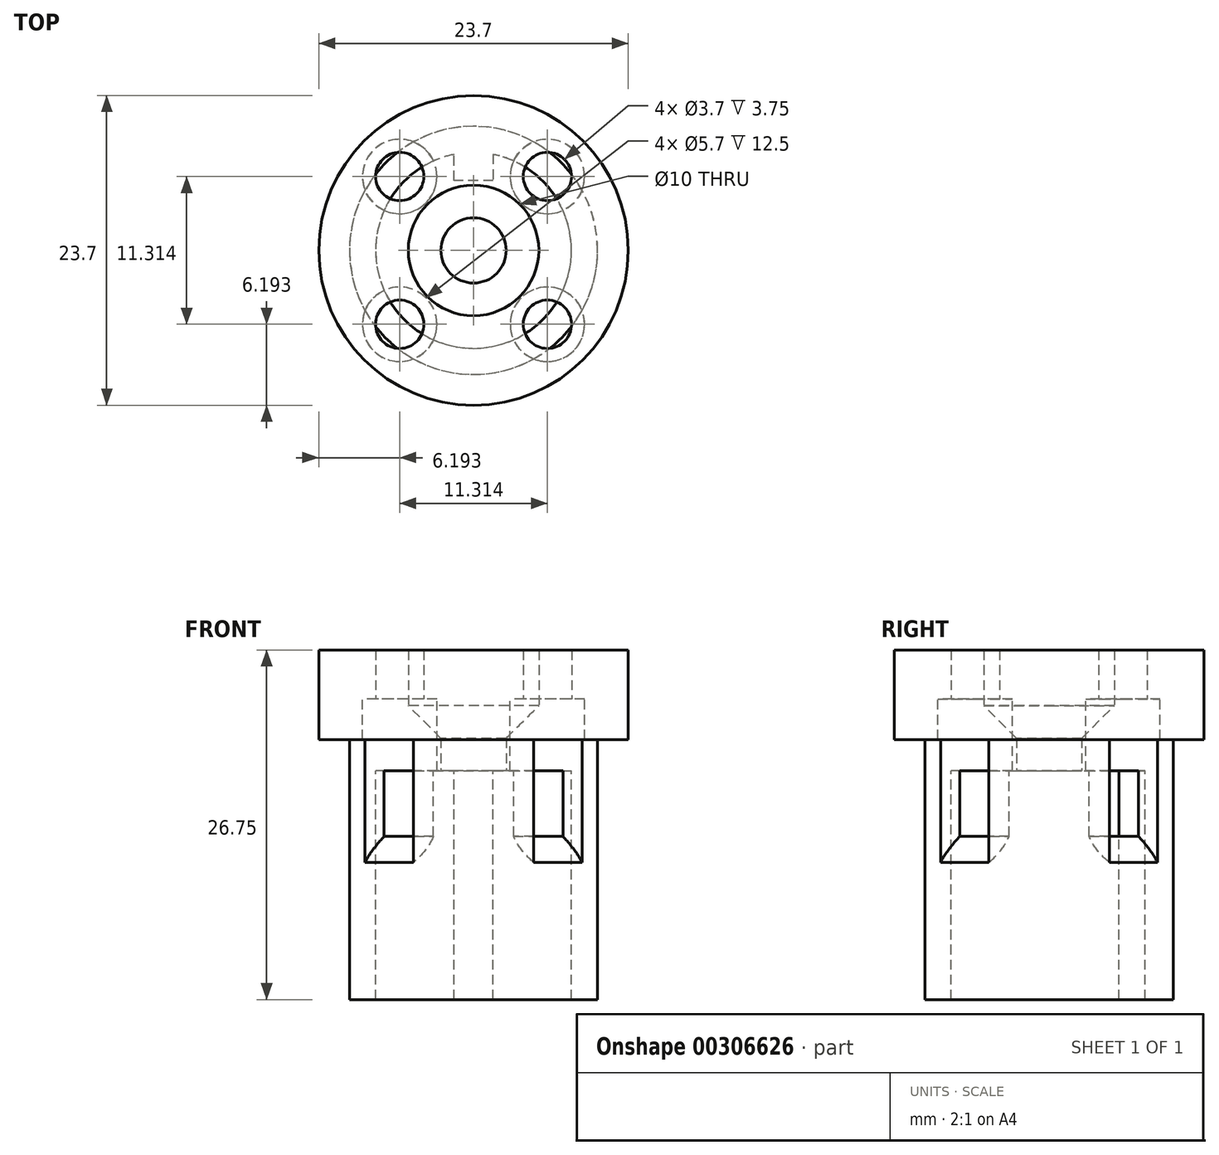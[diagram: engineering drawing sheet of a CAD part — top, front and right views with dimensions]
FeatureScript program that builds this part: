
annotation { "Feature Type Name" : "Feature", "Feature Type Description" : "" }
export const myFeature = defineFeature(function(context is Context, id is Id, definition is map)
    precondition{}
    {
        {
            var Q0;
            Q0=qCreatedBy(makeId("Top.planeOp"),FACE);
            var sketch = newSketch(context, id + "F0", { "sketchPlane" : qUnion([Q0])});
            skCircle(sketch, "E0", {"center": v(0, 0) * mm, "radius": 7.5 * mm});
            skPoint(sketch, "E1", {"position": v(-1.5, 7.35) * mm});
            skPoint(sketch, "E2", {"position": v(1.5, 7.35) * mm});
            skLineSegment(sketch, "E3", {"start": v(-1.5, 7.35) * mm, "end": v(1.5, 7.35) * mm});
            skPoint(sketch, "E4", {"position": v(0, 7.35) * mm});
            skLineSegment(sketch, "E5", {"start": v(-1.5, 7.35) * mm, "end": v(-1.5, 5.35) * mm});
            skLineSegment(sketch, "E6", {"start": v(-1.5, 5.35) * mm, "end": v(1.5, 5.35) * mm});
            skLineSegment(sketch, "E7", {"start": v(1.5, 5.35) * mm, "end": v(1.5, 7.35) * mm});
            skCircle(sketch, "E8", {"center": v(0, 0) * mm, "radius": 2.5 * mm});
            skCircle(sketch, "E9", {"center": v(0, 0) * mm, "radius": 9.5 * mm});
            skSolve(sketch);
        }
        {
            var Q0;
            Q0=qCreatedBy(makeId("Top.planeOp"),FACE);
            var sketch = newSketch(context, id + "F1", { "sketchPlane" : qUnion([Q0])});
            skCircle(sketch, "E10", {"center": v(0, 0) * mm, "radius": 2.5 * mm});
            skLineSegment(sketch, "E11", {"start": v(-2, 1.5) * mm, "end": v(2, 1.5) * mm});
            skCircle(sketch, "E12", {"center": v(0, 0) * mm, "radius": 4.5 * mm});
            skSolve(sketch);
        }
        {
            var Q0;
            Q0=makeQuery(id+"F0.imprint","IMPRINT",FACE,{"disambiguationData":[TD([[makeQuery(id+"F0.imprint","IMPRINT",EDGE,{"derivedFrom":sQuery(id+"F0.wireOp",EDGE,"E9")}),1.0]])]});
            var Q1;
            {var subQ0=sQuery(id+"F0.wireOp",EDGE,"E3");Q1=makeQuery(id+"F0.imprint","IMPRINT",FACE,{"disambiguationData":[TD([[makeQuery(id+"F0.imprint","IMPRINT",EDGE,{"derivedFrom":subQ0}),1.0]])]});}
            var Q2;
            Q2=makeQuery(id+"F0.imprint","IMPRINT",FACE,{"disambiguationData":[TD([[makeQuery(id+"F0.imprint","IMPRINT",EDGE,{"derivedFrom":sQuery(id+"F0.wireOp",EDGE,"E3")}),-1.0]])]});
            extrude(context, id + "F2", {"entities" : qUnion([Q0, Q1, Q2]), "oppositeDirection" : true, "depth" : 20 * mm});
        }
        {
            var Q0;
            Q0=makeQuery(id+"F1.imprint","IMPRINT",FACE,{"disambiguationData":[TD([[makeQuery(id+"F1.imprint","IMPRINT",EDGE,{"derivedFrom":sQuery(id+"F1.wireOp",EDGE,"E12")}),1.0]])]});
            extrude(context, id + "F3", {"entities" : qUnion([Q0]), "operationType" : NewBodyOperationType.ADD, "depth" : 3 * mm});
        }
        {
            var Q0;
            {var subQ1=sQuery(id+"F0.wireOp",EDGE,"E5");Q0=makeQuery(id+"F0.imprint","IMPRINT",FACE,{"disambiguationData":[TD([[makeQuery(id+"F0.imprint","IMPRINT",EDGE,{"derivedFrom":subQ1}),-1.0]])]});}
            var Q1;
            {var subQ0=sQuery(id+"F0.wireOp",EDGE,"E3");Q1=makeQuery(id+"F0.imprint","IMPRINT",FACE,{"disambiguationData":[TD([[makeQuery(id+"F0.imprint","IMPRINT",EDGE,{"derivedFrom":subQ0}),1.0]])]});}
            var Q2;
            Q2=makeQuery(id+"F0.imprint","IMPRINT",FACE,{"disambiguationData":[TD([[makeQuery(id+"F0.imprint","IMPRINT",EDGE,{"derivedFrom":sQuery(id+"F0.wireOp",EDGE,"E3")}),-1.0]])]});
            extrude(context, id + "F4", {"entities" : qUnion([Q0, Q1, Q2]), "operationType" : NewBodyOperationType.ADD, "endBound" : BoundingType.SYMMETRIC, "depth" : 5 * mm});
        }
        {
            var Q0;
            Q0=makeQuery(id+"F3.opExtrude","CAP_FACE",FACE,{"disambiguationData":[OSD([sQuery(id+"F1.wireOp",EDGE,"E10"),sQuery(id+"F1.wireOp",EDGE,"E11"),sQuery(id+"F1.wireOp",EDGE,"E12")])],"isStart":false});
            var sketch = newSketch(context, id + "F5", { "sketchPlane" : qUnion([Q0])});
            skCircle(sketch, "E13", {"center": v(0, 0) * mm, "radius": 8 * mm});
            skCircle(sketch, "E14", {"center": v(0, 0) * mm, "radius": 4 * mm});
            skLineSegment(sketch, "E15", {"start": v(5.66, -5.66) * mm, "end": v(-5.66, 5.66) * mm, "construction": true});
            skLineSegment(sketch, "E16", {"start": v(-5.66, -5.66) * mm, "end": v(5.66, 5.66) * mm, "construction": true});
            skLineSegment(sketch, "E17", {"start": v(-8, 0) * mm, "end": v(8, 0) * mm, "construction": true});
            skCircle(sketch, "E18", {"center": v(-5.66, 5.66) * mm, "radius": 1.85 * mm});
            skCircle(sketch, "E19", {"center": v(5.66, 5.66) * mm, "radius": 1.85 * mm});
            skCircle(sketch, "E20", {"center": v(-5.66, -5.66) * mm, "radius": 1.85 * mm});
            skCircle(sketch, "E21", {"center": v(5.66, -5.66) * mm, "radius": 1.85 * mm});
            skCircle(sketch, "E22", {"center": v(0, 0) * mm, "radius": 11.85 * mm});
            skCircle(sketch, "E23", {"center": v(-5.66, 5.66) * mm, "radius": 2.85 * mm});
            skCircle(sketch, "E24", {"center": v(5.66, 5.66) * mm, "radius": 2.85 * mm});
            skCircle(sketch, "E25", {"center": v(-5.66, -5.66) * mm, "radius": 2.85 * mm});
            skCircle(sketch, "E26", {"center": v(5.66, -5.66) * mm, "radius": 2.85 * mm});
            skSolve(sketch);
        }
        {
            var Q0;
            Q0=makeQuery(id+"F5.imprint","IMPRINT",FACE,{"disambiguationData":[TD([[makeQuery(id+"F5.imprint","IMPRINT",EDGE,{"derivedFrom":makeQuery(id+"F3.opExtrude","CAP_EDGE",EDGE,{"disambiguationData":[OSD([sQuery(id+"F1.wireOp",EDGE,"E12")])],"isStart":false})}),-1.0]])]});
            var Q1;
            Q1=makeQuery(id+"F5.imprint","IMPRINT",FACE,{"disambiguationData":[TD([[makeQuery(id+"F5.imprint","IMPRINT",EDGE,{"derivedFrom":sQuery(id+"F5.wireOp",EDGE,"E22")}),1.0]])]});
            var Q2;
            {var subQ0=sQuery(id+"F5.wireOp",EDGE,"E23");var subQ1=sQuery(id+"F5.wireOp",EDGE,"E13");var subQ2=makeQuery(id+"F5.imprint","INTERSECT",VERTEX,{"disambiguationData":[OD(0.0)],"derivedFrom":[subQ1,subQ0]});Q2=makeQuery(id+"F5.imprint","IMPRINT",FACE,{"disambiguationData":[TD([[makeQuery(id+"F5.imprint","IMPRINT",EDGE,{"disambiguationData":[TD([[subQ2,-1.0]])],"derivedFrom":subQ1}),-1.0]])]});}
            var Q3;
            {var subQ0=sQuery(id+"F5.wireOp",EDGE,"E23");var subQ1=sQuery(id+"F5.wireOp",EDGE,"E13");var subQ2=makeQuery(id+"F5.imprint","INTERSECT",VERTEX,{"disambiguationData":[OD(0.0)],"derivedFrom":[subQ1,subQ0]});Q3=makeQuery(id+"F5.imprint","IMPRINT",FACE,{"disambiguationData":[TD([[makeQuery(id+"F5.imprint","IMPRINT",EDGE,{"disambiguationData":[TD([[subQ2,-1.0]])],"derivedFrom":subQ1}),1.0]])]});}
            var Q4;
            {var subQ0=sQuery(id+"F5.wireOp",EDGE,"E19");var subQ1=sQuery(id+"F5.wireOp",EDGE,"E13");var subQ2=makeQuery(id+"F5.imprint","INTERSECT",VERTEX,{"disambiguationData":[OD(0.0)],"derivedFrom":[subQ1,subQ0]});Q4=makeQuery(id+"F5.imprint","IMPRINT",FACE,{"disambiguationData":[TD([[makeQuery(id+"F5.imprint","IMPRINT",EDGE,{"disambiguationData":[TD([[subQ2,1.0]])],"derivedFrom":subQ1}),-1.0]])]});}
            var Q5;
            {var subQ0=sQuery(id+"F5.wireOp",EDGE,"E19");var subQ1=sQuery(id+"F5.wireOp",EDGE,"E13");var subQ2=makeQuery(id+"F5.imprint","INTERSECT",VERTEX,{"disambiguationData":[OD(0.0)],"derivedFrom":[subQ1,subQ0]});Q5=makeQuery(id+"F5.imprint","IMPRINT",FACE,{"disambiguationData":[TD([[makeQuery(id+"F5.imprint","IMPRINT",EDGE,{"disambiguationData":[TD([[subQ2,1.0]])],"derivedFrom":subQ1}),1.0]])]});}
            var Q6;
            {var subQ0=sQuery(id+"F5.wireOp",EDGE,"E26");var subQ1=sQuery(id+"F5.wireOp",EDGE,"E13");var subQ2=makeQuery(id+"F5.imprint","INTERSECT",VERTEX,{"disambiguationData":[OD(0.0)],"derivedFrom":[subQ1,subQ0]});Q6=makeQuery(id+"F5.imprint","IMPRINT",FACE,{"disambiguationData":[TD([[makeQuery(id+"F5.imprint","IMPRINT",EDGE,{"disambiguationData":[TD([[subQ2,-1.0]])],"derivedFrom":subQ1}),-1.0]])]});}
            var Q7;
            {var subQ0=sQuery(id+"F5.wireOp",EDGE,"E26");var subQ1=sQuery(id+"F5.wireOp",EDGE,"E13");var subQ2=makeQuery(id+"F5.imprint","INTERSECT",VERTEX,{"disambiguationData":[OD(0.0)],"derivedFrom":[subQ1,subQ0]});Q7=makeQuery(id+"F5.imprint","IMPRINT",FACE,{"disambiguationData":[TD([[makeQuery(id+"F5.imprint","IMPRINT",EDGE,{"disambiguationData":[TD([[subQ2,-1.0]])],"derivedFrom":subQ1}),1.0]])]});}
            var Q8;
            {var subQ0=sQuery(id+"F5.wireOp",EDGE,"E25");var subQ1=sQuery(id+"F5.wireOp",EDGE,"E13");var subQ2=makeQuery(id+"F5.imprint","INTERSECT",VERTEX,{"disambiguationData":[OD(0.0)],"derivedFrom":[subQ1,subQ0]});Q8=makeQuery(id+"F5.imprint","IMPRINT",FACE,{"disambiguationData":[TD([[makeQuery(id+"F5.imprint","IMPRINT",EDGE,{"disambiguationData":[TD([[subQ2,-1.0]])],"derivedFrom":subQ1}),-1.0]])]});}
            var Q9;
            {var subQ0=sQuery(id+"F5.wireOp",EDGE,"E25");var subQ1=sQuery(id+"F5.wireOp",EDGE,"E13");var subQ2=makeQuery(id+"F5.imprint","INTERSECT",VERTEX,{"disambiguationData":[OD(0.0)],"derivedFrom":[subQ1,subQ0]});Q9=makeQuery(id+"F5.imprint","IMPRINT",FACE,{"disambiguationData":[TD([[makeQuery(id+"F5.imprint","IMPRINT",EDGE,{"disambiguationData":[TD([[subQ2,-1.0]])],"derivedFrom":subQ1}),1.0]])]});}
            extrude(context, id + "F6", {"entities" : qUnion([Q0, Q1, Q2, Q3, Q4, Q5, Q6, Q7, Q8, Q9]), "operationType" : NewBodyOperationType.ADD, "endBound" : BoundingType.SYMMETRIC, "depth" : 2.5 * mm});
        }
        {
            var Q0;
            Q0 = qSketchRegion(id + "F5", true);
            var Q1;
            Q1=makeQuery(id+"F6.opExtrude","CAP_FACE",FACE,{"disambiguationData":[OSD([sQuery(id+"F1.wireOp",EDGE,"E12"),sQuery(id+"F5.wireOp",EDGE,"E18"),sQuery(id+"F5.wireOp",EDGE,"E19"),sQuery(id+"F5.wireOp",EDGE,"E20"),sQuery(id+"F5.wireOp",EDGE,"E21"),sQuery(id+"F5.wireOp",EDGE,"E22")])],"isStart":false});
            extrude(context, id + "F7", {"entities" : qUnion([Q0, Q1]), "operationType" : NewBodyOperationType.ADD, "depth" : 2.5 * mm});
        }
        {
            var Q0;
            Q0=qCreatedBy(makeId("Top.planeOp"),FACE);
            var sketch = newSketch(context, id + "F8", { "sketchPlane" : qUnion([Q0])});
            skCircle(sketch, "E27", {"center": v(0, 0) * mm, "radius": 5 * mm});
            skCircle(sketch, "E28", {"center": v(0, 0) * mm, "radius": 2.5 * mm});
            skSolve(sketch);
        }
        {
            var Q0;
            Q0=makeQuery(id+"F8.imprint","IMPRINT",FACE,{"disambiguationData":[TD([[makeQuery(id+"F8.imprint","IMPRINT",EDGE,{"derivedFrom":sQuery(id+"F8.wireOp",EDGE,"E27")}),1.0]])]});
            extrude(context, id + "F9", {"entities" : qUnion([Q0]), "operationType" : NewBodyOperationType.ADD, "oppositeDirection" : true, "depth" : 2.5 * mm});
        }
        {
            var Q0;
            Q0=makeQuery(id+"F5.imprint","IMPRINT",FACE,{"disambiguationData":[TD([[makeQuery(id+"F5.imprint","IMPRINT",EDGE,{"derivedFrom":sQuery(id+"F5.wireOp",EDGE,"E22")}),1.0]])]});
            var Q1;
            Q1=makeQuery(id+"F5.imprint","IMPRINT",FACE,{"disambiguationData":[TD([[makeQuery(id+"F5.imprint","IMPRINT",EDGE,{"derivedFrom":makeQuery(id+"F3.opExtrude","CAP_EDGE",EDGE,{"disambiguationData":[OSD([sQuery(id+"F1.wireOp",EDGE,"E12")])],"isStart":false})}),-1.0]])]});
            extrude(context, id + "F10", {"entities" : qUnion([Q0, Q1]), "operationType" : NewBodyOperationType.ADD, "oppositeDirection" : true, "depth" : 3.1 * mm});
        }
        {
            var Q0;
            Q0=makeQuery(id+"F8.imprint","IMPRINT",FACE,{"disambiguationData":[TD([[makeQuery(id+"F8.imprint","IMPRINT",EDGE,{"derivedFrom":sQuery(id+"F8.wireOp",EDGE,"E27")}),1.0]])]});
            extrude(context, id + "F11", {"entities" : qUnion([Q0]), "operationType" : NewBodyOperationType.REMOVE, "depth" : 10 * mm});
        }
        {
            var Q0;
            {var subQ0=sQuery(id+"F5.wireOp",EDGE,"E23");var subQ1=sQuery(id+"F5.wireOp",EDGE,"E13");var subQ2=makeQuery(id+"F5.imprint","INTERSECT",VERTEX,{"disambiguationData":[OD(0.0)],"derivedFrom":[subQ1,subQ0]});Q0=makeQuery(id+"F5.imprint","IMPRINT",FACE,{"disambiguationData":[TD([[makeQuery(id+"F5.imprint","IMPRINT",EDGE,{"disambiguationData":[TD([[subQ2,-1.0]])],"derivedFrom":subQ1}),-1.0]])]});}
            var Q1;
            {var subQ0=sQuery(id+"F5.wireOp",EDGE,"E25");var subQ1=sQuery(id+"F5.wireOp",EDGE,"E13");var subQ2=makeQuery(id+"F5.imprint","INTERSECT",VERTEX,{"disambiguationData":[OD(0.0)],"derivedFrom":[subQ1,subQ0]});Q1=makeQuery(id+"F5.imprint","IMPRINT",FACE,{"disambiguationData":[TD([[makeQuery(id+"F5.imprint","IMPRINT",EDGE,{"disambiguationData":[TD([[subQ2,-1.0]])],"derivedFrom":subQ1}),-1.0]])]});}
            var Q2;
            {var subQ0=sQuery(id+"F5.wireOp",EDGE,"E26");var subQ1=sQuery(id+"F5.wireOp",EDGE,"E13");var subQ2=makeQuery(id+"F5.imprint","INTERSECT",VERTEX,{"disambiguationData":[OD(0.0)],"derivedFrom":[subQ1,subQ0]});Q2=makeQuery(id+"F5.imprint","IMPRINT",FACE,{"disambiguationData":[TD([[makeQuery(id+"F5.imprint","IMPRINT",EDGE,{"disambiguationData":[TD([[subQ2,-1.0]])],"derivedFrom":subQ1}),-1.0]])]});}
            var Q3;
            {var subQ0=sQuery(id+"F5.wireOp",EDGE,"E19");var subQ1=sQuery(id+"F5.wireOp",EDGE,"E13");var subQ2=makeQuery(id+"F5.imprint","INTERSECT",VERTEX,{"disambiguationData":[OD(0.0)],"derivedFrom":[subQ1,subQ0]});Q3=makeQuery(id+"F5.imprint","IMPRINT",FACE,{"disambiguationData":[TD([[makeQuery(id+"F5.imprint","IMPRINT",EDGE,{"disambiguationData":[TD([[subQ2,1.0]])],"derivedFrom":subQ1}),-1.0]])]});}
            var Q4;
            {var subQ0=sQuery(id+"F5.wireOp",EDGE,"E23");var subQ1=sQuery(id+"F5.wireOp",EDGE,"E13");var subQ2=makeQuery(id+"F5.imprint","INTERSECT",VERTEX,{"disambiguationData":[OD(0.0)],"derivedFrom":[subQ1,subQ0]});Q4=makeQuery(id+"F5.imprint","IMPRINT",FACE,{"disambiguationData":[TD([[makeQuery(id+"F5.imprint","IMPRINT",EDGE,{"disambiguationData":[TD([[subQ2,-1.0]])],"derivedFrom":subQ1}),1.0]])]});}
            var Q5;
            {var subQ0=sQuery(id+"F5.wireOp",EDGE,"E25");var subQ1=sQuery(id+"F5.wireOp",EDGE,"E13");var subQ2=makeQuery(id+"F5.imprint","INTERSECT",VERTEX,{"disambiguationData":[OD(0.0)],"derivedFrom":[subQ1,subQ0]});Q5=makeQuery(id+"F5.imprint","IMPRINT",FACE,{"disambiguationData":[TD([[makeQuery(id+"F5.imprint","IMPRINT",EDGE,{"disambiguationData":[TD([[subQ2,-1.0]])],"derivedFrom":subQ1}),1.0]])]});}
            var Q6;
            {var subQ0=sQuery(id+"F5.wireOp",EDGE,"E19");var subQ1=sQuery(id+"F5.wireOp",EDGE,"E13");var subQ2=makeQuery(id+"F5.imprint","INTERSECT",VERTEX,{"disambiguationData":[OD(0.0)],"derivedFrom":[subQ1,subQ0]});Q6=makeQuery(id+"F5.imprint","IMPRINT",FACE,{"disambiguationData":[TD([[makeQuery(id+"F5.imprint","IMPRINT",EDGE,{"disambiguationData":[TD([[subQ2,1.0]])],"derivedFrom":subQ1}),1.0]])]});}
            var Q7;
            {var subQ0=sQuery(id+"F5.wireOp",EDGE,"E26");var subQ1=sQuery(id+"F5.wireOp",EDGE,"E13");var subQ2=makeQuery(id+"F5.imprint","INTERSECT",VERTEX,{"disambiguationData":[OD(0.0)],"derivedFrom":[subQ1,subQ0]});Q7=makeQuery(id+"F5.imprint","IMPRINT",FACE,{"disambiguationData":[TD([[makeQuery(id+"F5.imprint","IMPRINT",EDGE,{"disambiguationData":[TD([[subQ2,-1.0]])],"derivedFrom":subQ1}),1.0]])]});}
            var Q8;
            {var subQ0=sQuery(id+"F5.wireOp",EDGE,"E18");var subQ1=sQuery(id+"F5.wireOp",EDGE,"E13");var subQ2=makeQuery(id+"F5.imprint","INTERSECT",VERTEX,{"disambiguationData":[OD(0.0)],"derivedFrom":[subQ1,subQ0]});Q8=makeQuery(id+"F5.imprint","IMPRINT",FACE,{"disambiguationData":[TD([[makeQuery(id+"F5.imprint","IMPRINT",EDGE,{"disambiguationData":[TD([[subQ2,-1.0]])],"derivedFrom":subQ1}),1.0]])]});}
            var Q9;
            {var subQ0=sQuery(id+"F5.wireOp",EDGE,"E18");var subQ1=sQuery(id+"F5.wireOp",EDGE,"E13");var subQ2=makeQuery(id+"F5.imprint","INTERSECT",VERTEX,{"disambiguationData":[OD(0.0)],"derivedFrom":[subQ1,subQ0]});Q9=makeQuery(id+"F5.imprint","IMPRINT",FACE,{"disambiguationData":[TD([[makeQuery(id+"F5.imprint","IMPRINT",EDGE,{"disambiguationData":[TD([[subQ2,-1.0]])],"derivedFrom":subQ1}),-1.0]])]});}
            var Q10;
            {var subQ0=sQuery(id+"F5.wireOp",EDGE,"E19");var subQ1=sQuery(id+"F5.wireOp",EDGE,"E13");var subQ2=makeQuery(id+"F5.imprint","INTERSECT",VERTEX,{"disambiguationData":[OD(0.0)],"derivedFrom":[subQ1,subQ0]});Q10=makeQuery(id+"F5.imprint","IMPRINT",FACE,{"disambiguationData":[TD([[makeQuery(id+"F5.imprint","IMPRINT",EDGE,{"disambiguationData":[TD([[subQ2,-1.0]])],"derivedFrom":subQ1}),1.0]])]});}
            var Q11;
            {var subQ0=sQuery(id+"F5.wireOp",EDGE,"E19");var subQ1=sQuery(id+"F5.wireOp",EDGE,"E13");var subQ2=makeQuery(id+"F5.imprint","INTERSECT",VERTEX,{"disambiguationData":[OD(0.0)],"derivedFrom":[subQ1,subQ0]});Q11=makeQuery(id+"F5.imprint","IMPRINT",FACE,{"disambiguationData":[TD([[makeQuery(id+"F5.imprint","IMPRINT",EDGE,{"disambiguationData":[TD([[subQ2,-1.0]])],"derivedFrom":subQ1}),-1.0]])]});}
            var Q12;
            {var subQ0=sQuery(id+"F5.wireOp",EDGE,"E21");var subQ1=sQuery(id+"F5.wireOp",EDGE,"E13");var subQ2=makeQuery(id+"F5.imprint","INTERSECT",VERTEX,{"disambiguationData":[OD(0.0)],"derivedFrom":[subQ1,subQ0]});Q12=makeQuery(id+"F5.imprint","IMPRINT",FACE,{"disambiguationData":[TD([[makeQuery(id+"F5.imprint","IMPRINT",EDGE,{"disambiguationData":[TD([[subQ2,-1.0]])],"derivedFrom":subQ1}),1.0]])]});}
            var Q13;
            {var subQ0=sQuery(id+"F5.wireOp",EDGE,"E21");var subQ1=sQuery(id+"F5.wireOp",EDGE,"E13");var subQ2=makeQuery(id+"F5.imprint","INTERSECT",VERTEX,{"disambiguationData":[OD(0.0)],"derivedFrom":[subQ1,subQ0]});Q13=makeQuery(id+"F5.imprint","IMPRINT",FACE,{"disambiguationData":[TD([[makeQuery(id+"F5.imprint","IMPRINT",EDGE,{"disambiguationData":[TD([[subQ2,-1.0]])],"derivedFrom":subQ1}),-1.0]])]});}
            var Q14;
            {var subQ0=sQuery(id+"F5.wireOp",EDGE,"E20");var subQ1=sQuery(id+"F5.wireOp",EDGE,"E13");var subQ2=makeQuery(id+"F5.imprint","INTERSECT",VERTEX,{"disambiguationData":[OD(0.0)],"derivedFrom":[subQ1,subQ0]});Q14=makeQuery(id+"F5.imprint","IMPRINT",FACE,{"disambiguationData":[TD([[makeQuery(id+"F5.imprint","IMPRINT",EDGE,{"disambiguationData":[TD([[subQ2,-1.0]])],"derivedFrom":subQ1}),1.0]])]});}
            var Q15;
            {var subQ0=sQuery(id+"F5.wireOp",EDGE,"E20");var subQ1=sQuery(id+"F5.wireOp",EDGE,"E13");var subQ2=makeQuery(id+"F5.imprint","INTERSECT",VERTEX,{"disambiguationData":[OD(0.0)],"derivedFrom":[subQ1,subQ0]});Q15=makeQuery(id+"F5.imprint","IMPRINT",FACE,{"disambiguationData":[TD([[makeQuery(id+"F5.imprint","IMPRINT",EDGE,{"disambiguationData":[TD([[subQ2,-1.0]])],"derivedFrom":subQ1}),-1.0]])]});}
            extrude(context, id + "F12", {"entities" : qUnion([Q0, Q1, Q2, Q3, Q4, Q5, Q6, Q7, Q8, Q9, Q10, Q11, Q12, Q13, Q14, Q15]), "operationType" : NewBodyOperationType.REMOVE, "oppositeDirection" : true, "depth" : 7.5 * mm});
        }
        {
            var Q0;
            Q0=makeQuery(id+"F12.boolean.opBoolean","INTERSECT",EDGE,{"derivedFrom":[makeQuery(id+"F2.opExtrude","SWEPT_FACE",FACE,{"disambiguationData":[OSD([sQuery(id+"F0.wireOp",EDGE,"E9")])]}),makeQuery(id+"F12.opExtrude","CAP_FACE",FACE,{"disambiguationData":[OSD([sQuery(id+"F5.wireOp",EDGE,"E23")])],"isStart":false})]});
            var Q1;
            Q1=makeQuery(id+"F12.boolean.opBoolean","INTERSECT",EDGE,{"derivedFrom":[makeQuery(id+"F2.opExtrude","SWEPT_FACE",FACE,{"disambiguationData":[OSD([sQuery(id+"F0.wireOp",EDGE,"E9")])]}),makeQuery(id+"F12.opExtrude","CAP_FACE",FACE,{"disambiguationData":[OSD([sQuery(id+"F5.wireOp",EDGE,"E25")])],"isStart":false})]});
            var Q2;
            Q2=makeQuery(id+"F12.boolean.opBoolean","INTERSECT",EDGE,{"derivedFrom":[makeQuery(id+"F2.opExtrude","SWEPT_FACE",FACE,{"disambiguationData":[OSD([sQuery(id+"F0.wireOp",EDGE,"E9")])]}),makeQuery(id+"F12.opExtrude","CAP_FACE",FACE,{"disambiguationData":[OSD([sQuery(id+"F5.wireOp",EDGE,"E26")])],"isStart":false})]});
            var Q3;
            Q3=makeQuery(id+"F12.boolean.opBoolean","INTERSECT",EDGE,{"derivedFrom":[makeQuery(id+"F2.opExtrude","SWEPT_FACE",FACE,{"disambiguationData":[OSD([sQuery(id+"F0.wireOp",EDGE,"E9")])]}),makeQuery(id+"F12.opExtrude","CAP_FACE",FACE,{"disambiguationData":[OSD([sQuery(id+"F5.wireOp",EDGE,"E24")])],"isStart":false})]});
            chamfer(context, id + "F13", {"entities" : qUnion([Q0, Q1, Q2, Q3]), "width" : 5 * mm, "tangentPropagation" : true});
        }
        {
            var Q0;
            Q0=makeQuery(id+"F11.boolean.opBoolean","COPY",EDGE,{"derivedFrom":makeQuery(id+"F11.opExtrude","CAP_EDGE",EDGE,{"disambiguationData":[OSD([sQuery(id+"F8.wireOp",EDGE,"E27")])],"isStart":true})});
            chamfer(context, id + "F14", {"entities" : qUnion([Q0]), "width" : 2.5 * mm, "tangentPropagation" : true});
        }
    });
